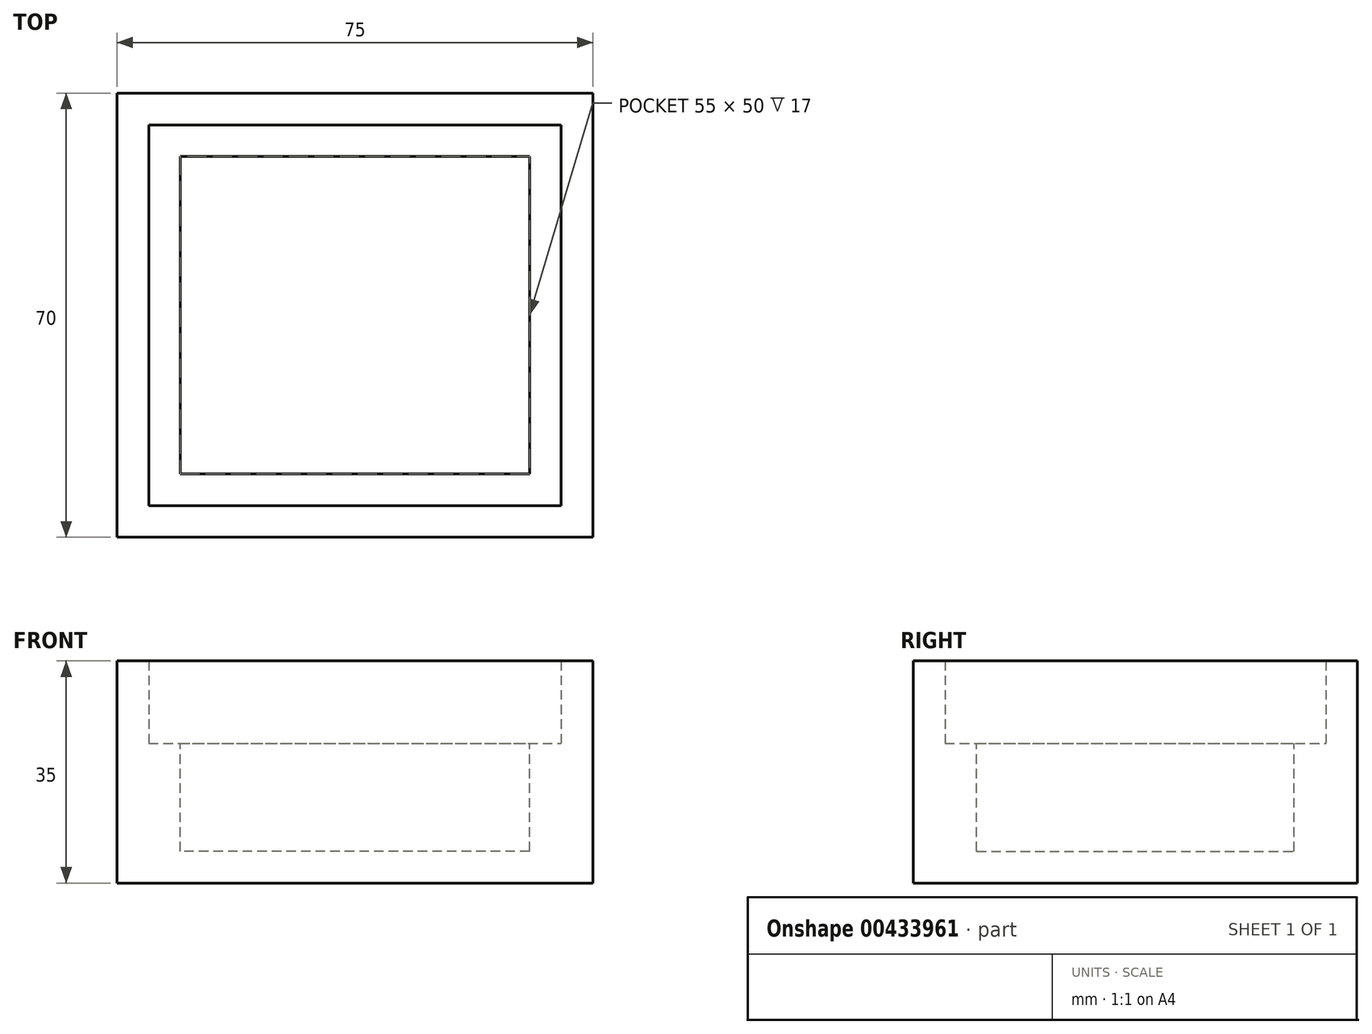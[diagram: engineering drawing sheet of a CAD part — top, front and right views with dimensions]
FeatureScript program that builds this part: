
annotation { "Feature Type Name" : "Feature", "Feature Type Description" : "" }
export const myFeature = defineFeature(function(context is Context, id is Id, definition is map)
    precondition{}
    {
        {
            var Q0;
            Q0=qCreatedBy(makeId("Top.planeOp"),FACE);
            var sketch = newSketch(context, id + "F0", { "sketchPlane" : qUnion([Q0])});
            skLineSegment(sketch, "E0.bottom", {"start": v(-37.5, -35) * mm, "end": v(37.5, -35) * mm});
            skLineSegment(sketch, "E0.top", {"start": v(-37.5, 35) * mm, "end": v(37.5, 35) * mm});
            skLineSegment(sketch, "E0.left", {"start": v(-37.5, -35) * mm, "end": v(-37.5, 35) * mm});
            skLineSegment(sketch, "E0.right", {"start": v(37.5, -35) * mm, "end": v(37.5, 35) * mm});
            skPoint(sketch, "E0.middle", {"position": v(0, 0) * mm});
            skLineSegment(sketch, "E1.0", {"start": v(-32.5, -30) * mm, "end": v(-32.5, 30) * mm});
            skLineSegment(sketch, "E1.1", {"start": v(-32.5, -30) * mm, "end": v(32.5, -30) * mm});
            skLineSegment(sketch, "E1.2", {"start": v(32.5, -30) * mm, "end": v(32.5, 30) * mm});
            skLineSegment(sketch, "E1.3", {"start": v(-32.5, 30) * mm, "end": v(32.5, 30) * mm});
            skSolve(sketch);
        }
        {
            var Q0;
            Q0=makeQuery(id+"F0.imprint","IMPRINT",FACE,{"disambiguationData":[TD([[makeQuery(id+"F0.imprint","IMPRINT",EDGE,{"derivedFrom":sQuery(id+"F0.wireOp",EDGE,"E0.bottom")}),1.0]])]});
            extrude(context, id + "F1", {"entities" : qUnion([Q0]), "depth" : 35 * mm});
        }
        {
            var Q0;
            Q0=makeQuery(id+"F0.imprint","IMPRINT",FACE,{"disambiguationData":[TD([[makeQuery(id+"F0.imprint","IMPRINT",EDGE,{"derivedFrom":sQuery(id+"F0.wireOp",EDGE,"E1.0")}),-1.0]])]});
            extrude(context, id + "F2", {"entities" : qUnion([Q0]), "operationType" : NewBodyOperationType.ADD, "depth" : 7 * mm});
        }
        {
            var Q0;
            Q0=makeQuery(id+"F0.imprint","IMPRINT",FACE,{"disambiguationData":[TD([[makeQuery(id+"F0.imprint","IMPRINT",EDGE,{"derivedFrom":sQuery(id+"F0.wireOp",EDGE,"E0.bottom")}),1.0]])]});
            var Q1;
            Q1=makeQuery(id+"F0.imprint","IMPRINT",FACE,{"disambiguationData":[TD([[makeQuery(id+"F0.imprint","IMPRINT",EDGE,{"derivedFrom":sQuery(id+"F0.wireOp",EDGE,"E1.0")}),-1.0]])]});
            extrude(context, id + "F3", {"entities" : qUnion([Q0, Q1]), "depth" : 15 * mm});
        }
        {
            var Q0;
            Q0=makeQuery(id+"F0.imprint","IMPRINT",FACE,{"disambiguationData":[TD([[makeQuery(id+"F0.imprint","IMPRINT",EDGE,{"derivedFrom":sQuery(id+"F0.wireOp",EDGE,"E1.0")}),-1.0]])]});
            extrude(context, id + "F4", {"entities" : qUnion([Q0]), "operationType" : NewBodyOperationType.ADD, "depth" : 22 * mm});
        }
        {
            var Q0;
            Q0=makeQuery(id+"F4.opExtrude","CAP_FACE",FACE,{"disambiguationData":[OSD([sQuery(id+"F0.wireOp",EDGE,"E1.0"),sQuery(id+"F0.wireOp",EDGE,"E1.1"),sQuery(id+"F0.wireOp",EDGE,"E1.2"),sQuery(id+"F0.wireOp",EDGE,"E1.3")])],"isStart":false});
            var sketch = newSketch(context, id + "F5", { "sketchPlane" : qUnion([Q0])});
            skLineSegment(sketch, "E2.0", {"start": v(27.5, 25) * mm, "end": v(-27.5, 25) * mm});
            skLineSegment(sketch, "E2.1", {"start": v(27.5, -25) * mm, "end": v(27.5, 25) * mm});
            skLineSegment(sketch, "E2.2", {"start": v(-27.5, -25) * mm, "end": v(27.5, -25) * mm});
            skLineSegment(sketch, "E2.3", {"start": v(-27.5, 25) * mm, "end": v(-27.5, -25) * mm});
            skSolve(sketch);
        }
        {
            var Q0;
            Q0=makeQuery(id+"F5.imprint","IMPRINT",FACE,{"disambiguationData":[TD([[makeQuery(id+"F5.imprint","IMPRINT",EDGE,{"derivedFrom":sQuery(id+"F5.wireOp",EDGE,"E2.0")}),1.0]])]});
            extrude(context, id + "F6", {"entities" : qUnion([Q0]), "operationType" : NewBodyOperationType.REMOVE, "oppositeDirection" : true, "depth" : 17 * mm});
        }
    });
